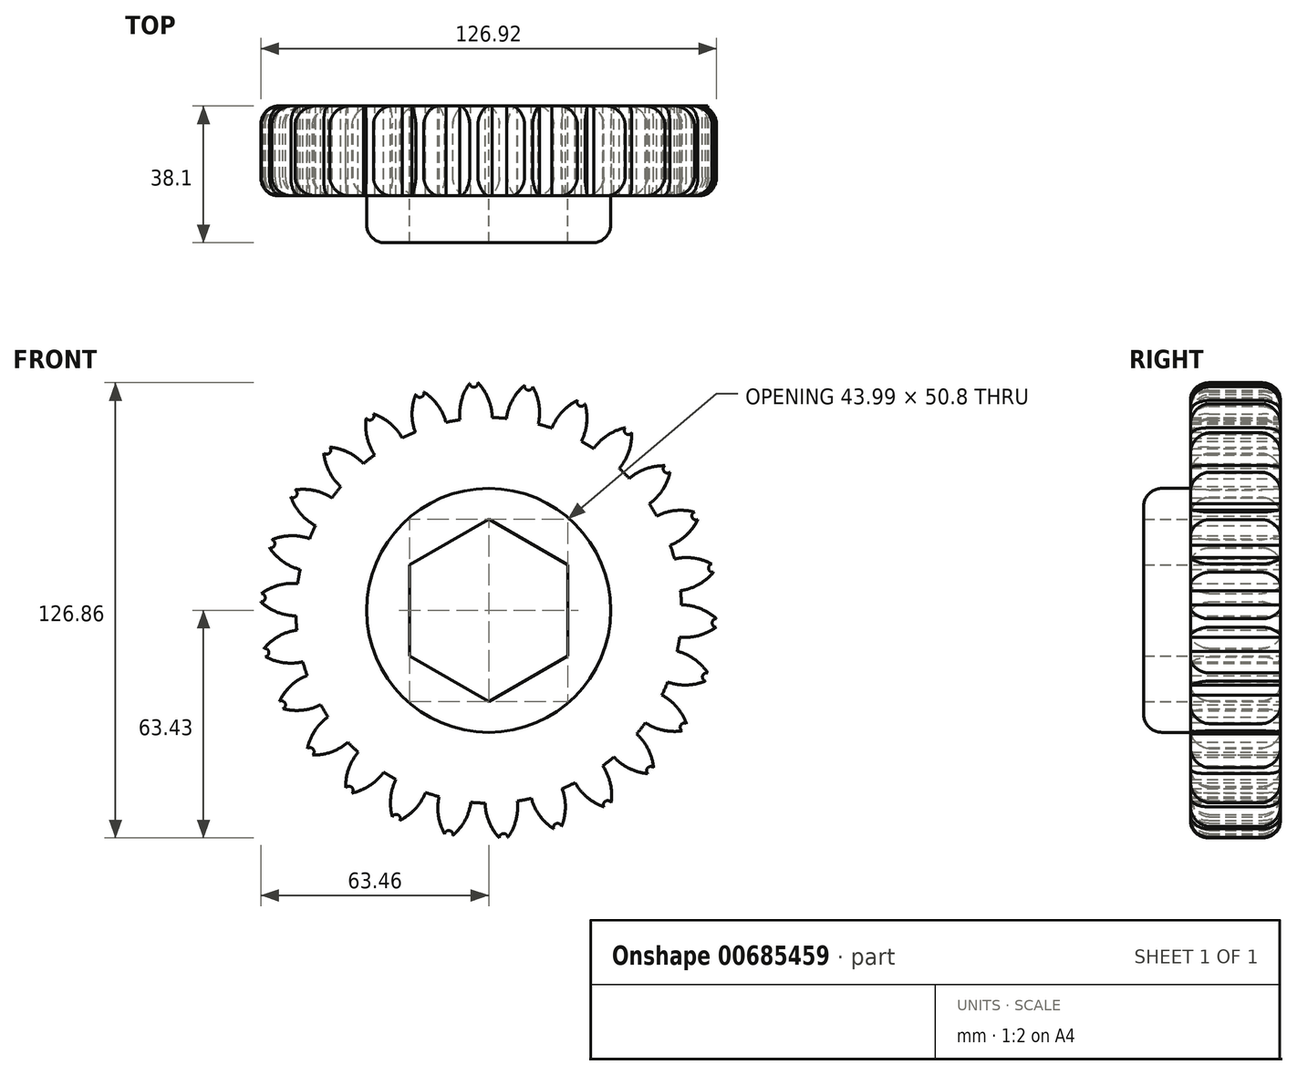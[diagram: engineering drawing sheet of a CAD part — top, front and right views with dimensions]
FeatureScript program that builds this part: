
annotation { "Feature Type Name" : "Feature", "Feature Type Description" : "" }
export const myFeature = defineFeature(function(context is Context, id is Id, definition is map)
    precondition{}
    {
        {
            var Q0;
            Q0=qCreatedBy(makeId("Front.planeOp"),FACE);
            var sketch = newSketch(context, id + "F0", { "sketchPlane" : qUnion([Q0])});
            skCircle(sketch, "E0", {"center": v(0, 0) * mm, "radius": 63.5 * mm, "construction": true});
            skCircle(sketch, "E1", {"center": v(0, 0) * mm, "radius": 58.67 * mm, "construction": true});
            skCircle(sketch, "E2", {"center": v(0, 0) * mm, "radius": 53.72 * mm});
            skLineSegment(sketch, "E3", {"start": v(0, 0) * mm, "end": v(0, 115.56) * mm, "construction": true});
            skLineSegment(sketch, "E4", {"start": v(0, 0) * mm, "end": v(-7.73, 117.88) * mm, "construction": true});
            skLineSegment(sketch, "E5", {"start": v(0, 58.67) * mm, "end": v(-76.77, 58.67) * mm, "construction": true});
            skLineSegment(sketch, "E6", {"start": v(0, 58.67) * mm, "end": v(-76.77, 30.73) * mm, "construction": true});
            skCircle(sketch, "E7", {"center": v(0, 0) * mm, "radius": 55.14 * mm, "construction": true});
            skCircle(sketch, "E8", {"center": v(0, 58.67) * mm, "radius": 14.6 * mm, "construction": true});
            skCircle(sketch, "E9", {"center": v(-13.63, 53.42) * mm, "radius": 14.6 * mm, "construction": true});
            skArc(sketch, "E10", {"start": v(0, 58.67) * mm, "mid": v(-1.27, 61.2) * mm, "end": v(-2.99, 63.43) * mm});
            skArc(sketch, "E11", {"start": v(0.97, 53.71) * mm, "mid": v(0.7, 56.24) * mm, "end": v(0, 58.67) * mm});
            skArc(sketch, "E12.MirrorCS", {"start": v(-7.66, 58.17) * mm, "mid": v(-6.73, 60.84) * mm, "end": v(-5.32, 63.28) * mm});
            skArc(sketch, "E13.MirrorCS", {"start": v(-7.98, 53.13) * mm, "mid": v(-8.04, 55.66) * mm, "end": v(-7.66, 58.17) * mm});
            skArc(sketch, "E14", {"start": v(-5.32, 63.28) * mm, "mid": v(-4.08, 62.2) * mm, "end": v(-2.99, 63.43) * mm});
            skPoint(sketch, "E15.0.midPoint", {"position": v(22.97, -13.77) * mm});
            skPoint(sketch, "E16.0.midPoint", {"position": v(19.49, -6.33) * mm});
            skCircle(sketch, "E17.cCircle", {"center": v(0, 0) * mm, "radius": 22 * mm, "construction": true});
            skLineSegment(sketch, "E17.0", {"start": v(22, 12.7) * mm, "end": v(22, -12.7) * mm});
            skLineSegment(sketch, "E17.1", {"start": v(22, -12.7) * mm, "end": v(0, -25.4) * mm});
            skLineSegment(sketch, "E17.2", {"start": v(0, -25.4) * mm, "end": v(-22, -12.7) * mm});
            skLineSegment(sketch, "E17.3", {"start": v(-22, -12.7) * mm, "end": v(-22, 12.7) * mm});
            skLineSegment(sketch, "E17.4", {"start": v(-22, 12.7) * mm, "end": v(0, 25.4) * mm});
            skLineSegment(sketch, "E17.5", {"start": v(0, 25.4) * mm, "end": v(22, 12.7) * mm});
            skPoint(sketch, "E17.0.midPoint", {"position": v(22, 0) * mm});
            skCircle(sketch, "E18", {"center": v(0, 0) * mm, "radius": 33.98 * mm});
            skSolve(sketch);
        }
        {
            var Q0;
            {var subQ0=sQuery(id+"F0.wireOp",EDGE,"E2");var subQ1=makeQuery(id+"F0.imprint","INTERSECT",VERTEX,{"derivedFrom":[subQ0,sQuery(id+"F0.wireOp",EDGE,"E11")]});Q0=makeQuery(id+"F0.imprint","IMPRINT",FACE,{"disambiguationData":[TD([[makeQuery(id+"F0.imprint","IMPRINT",EDGE,{"disambiguationData":[TD([[subQ1,-1.0]])],"derivedFrom":subQ0}),1.0]])]});}
            var Q1;
            Q1=makeQuery(id+"F0.imprint","IMPRINT",FACE,{"disambiguationData":[TD([[makeQuery(id+"F0.imprint","IMPRINT",EDGE,{"derivedFrom":sQuery(id+"F0.wireOp",EDGE,"E10")}),1.0]])]});
            extrude(context, id + "F1", {"entities" : qUnion([Q0, Q1]), "depth" : 25 * mm, "offsetDistance" : 25.4 * mm});
        }
        {
            var Q0;
            Q0=makeQuery(id+"F1.opExtrude","SWEPT_BODY",BODY,{"disambiguationData":[OSD([sQuery(id+"F0.wireOp",EDGE,"E2"),sQuery(id+"F0.wireOp",EDGE,"E10"),sQuery(id+"F0.wireOp",EDGE,"E11"),sQuery(id+"F0.wireOp",EDGE,"E12.MirrorCS"),sQuery(id+"F0.wireOp",EDGE,"E13.MirrorCS"),sQuery(id+"F0.wireOp",EDGE,"E14")])]});
            var Q1;
            Q1=makeQuery(id+"F1.opExtrude","SWEPT_FACE",FACE,{"disambiguationData":[OSD([sQuery(id+"F0.wireOp",EDGE,"E2")])]});
            circularPattern(context, id + "F2", {"entities" : qUnion([Q0]), "axis" : qUnion([Q1]), "angle" : 360 * degree, "instanceCount" : 26, "equalSpace" : true});
        }
        {
            var Q0;
            Q0=makeQuery(id+"F1.opExtrude","CAP_EDGE",EDGE,{"disambiguationData":[OSD([sQuery(id+"F0.wireOp",EDGE,"E14")])],"isStart":false});
            var Q1;
            Q1=makeQuery(id+"F1.opExtrude","CAP_EDGE",EDGE,{"disambiguationData":[OSD([sQuery(id+"F0.wireOp",EDGE,"E14")])],"isStart":true});
            var Q2;
            Q2=makeQuery(id+"F2.opPattern","COPY",EDGE,{"derivedFrom":makeQuery(id+"F1.opExtrude","CAP_EDGE",EDGE,{"disambiguationData":[OSD([sQuery(id+"F0.wireOp",EDGE,"E14")])],"isStart":false}),"instanceName":"25"});
            var Q3;
            Q3=makeQuery(id+"F2.opPattern","COPY",EDGE,{"derivedFrom":makeQuery(id+"F1.opExtrude","CAP_EDGE",EDGE,{"disambiguationData":[OSD([sQuery(id+"F0.wireOp",EDGE,"E14")])],"isStart":true}),"instanceName":"25"});
            var Q4;
            Q4=makeQuery(id+"F2.opPattern","COPY",EDGE,{"derivedFrom":makeQuery(id+"F1.opExtrude","CAP_EDGE",EDGE,{"disambiguationData":[OSD([sQuery(id+"F0.wireOp",EDGE,"E14")])],"isStart":true}),"instanceName":"24"});
            var Q5;
            Q5=makeQuery(id+"F2.opPattern","COPY",EDGE,{"derivedFrom":makeQuery(id+"F1.opExtrude","CAP_EDGE",EDGE,{"disambiguationData":[OSD([sQuery(id+"F0.wireOp",EDGE,"E14")])],"isStart":false}),"instanceName":"24"});
            var Q6;
            Q6=makeQuery(id+"F2.opPattern","COPY",EDGE,{"derivedFrom":makeQuery(id+"F1.opExtrude","CAP_EDGE",EDGE,{"disambiguationData":[OSD([sQuery(id+"F0.wireOp",EDGE,"E14")])],"isStart":false}),"instanceName":"23"});
            var Q7;
            Q7=makeQuery(id+"F2.opPattern","COPY",EDGE,{"derivedFrom":makeQuery(id+"F1.opExtrude","CAP_EDGE",EDGE,{"disambiguationData":[OSD([sQuery(id+"F0.wireOp",EDGE,"E14")])],"isStart":true}),"instanceName":"23"});
            var Q8;
            Q8=makeQuery(id+"F2.opPattern","COPY",EDGE,{"derivedFrom":makeQuery(id+"F1.opExtrude","CAP_EDGE",EDGE,{"disambiguationData":[OSD([sQuery(id+"F0.wireOp",EDGE,"E14")])],"isStart":false}),"instanceName":"22"});
            var Q9;
            Q9=makeQuery(id+"F2.opPattern","COPY",EDGE,{"derivedFrom":makeQuery(id+"F1.opExtrude","CAP_EDGE",EDGE,{"disambiguationData":[OSD([sQuery(id+"F0.wireOp",EDGE,"E14")])],"isStart":true}),"instanceName":"22"});
            var Q10;
            Q10=makeQuery(id+"F2.opPattern","COPY",EDGE,{"derivedFrom":makeQuery(id+"F1.opExtrude","CAP_EDGE",EDGE,{"disambiguationData":[OSD([sQuery(id+"F0.wireOp",EDGE,"E14")])],"isStart":true}),"instanceName":"21"});
            var Q11;
            Q11=makeQuery(id+"F2.opPattern","COPY",EDGE,{"derivedFrom":makeQuery(id+"F1.opExtrude","CAP_EDGE",EDGE,{"disambiguationData":[OSD([sQuery(id+"F0.wireOp",EDGE,"E14")])],"isStart":false}),"instanceName":"21"});
            var Q12;
            Q12=makeQuery(id+"F2.opPattern","COPY",EDGE,{"derivedFrom":makeQuery(id+"F1.opExtrude","CAP_EDGE",EDGE,{"disambiguationData":[OSD([sQuery(id+"F0.wireOp",EDGE,"E14")])],"isStart":true}),"instanceName":"20"});
            var Q13;
            Q13=makeQuery(id+"F2.opPattern","COPY",EDGE,{"derivedFrom":makeQuery(id+"F1.opExtrude","CAP_EDGE",EDGE,{"disambiguationData":[OSD([sQuery(id+"F0.wireOp",EDGE,"E14")])],"isStart":false}),"instanceName":"20"});
            var Q14;
            Q14=makeQuery(id+"F2.opPattern","COPY",EDGE,{"derivedFrom":makeQuery(id+"F1.opExtrude","CAP_EDGE",EDGE,{"disambiguationData":[OSD([sQuery(id+"F0.wireOp",EDGE,"E14")])],"isStart":true}),"instanceName":"19"});
            var Q15;
            Q15=makeQuery(id+"F2.opPattern","COPY",EDGE,{"derivedFrom":makeQuery(id+"F1.opExtrude","CAP_EDGE",EDGE,{"disambiguationData":[OSD([sQuery(id+"F0.wireOp",EDGE,"E14")])],"isStart":false}),"instanceName":"19"});
            var Q16;
            Q16=makeQuery(id+"F2.opPattern","COPY",EDGE,{"derivedFrom":makeQuery(id+"F1.opExtrude","CAP_EDGE",EDGE,{"disambiguationData":[OSD([sQuery(id+"F0.wireOp",EDGE,"E14")])],"isStart":true}),"instanceName":"18"});
            var Q17;
            Q17=makeQuery(id+"F2.opPattern","COPY",EDGE,{"derivedFrom":makeQuery(id+"F1.opExtrude","CAP_EDGE",EDGE,{"disambiguationData":[OSD([sQuery(id+"F0.wireOp",EDGE,"E14")])],"isStart":false}),"instanceName":"18"});
            var Q18;
            Q18=makeQuery(id+"F2.opPattern","COPY",EDGE,{"derivedFrom":makeQuery(id+"F1.opExtrude","CAP_EDGE",EDGE,{"disambiguationData":[OSD([sQuery(id+"F0.wireOp",EDGE,"E14")])],"isStart":true}),"instanceName":"17"});
            var Q19;
            Q19=makeQuery(id+"F2.opPattern","COPY",EDGE,{"derivedFrom":makeQuery(id+"F1.opExtrude","CAP_EDGE",EDGE,{"disambiguationData":[OSD([sQuery(id+"F0.wireOp",EDGE,"E14")])],"isStart":false}),"instanceName":"17"});
            var Q20;
            Q20=makeQuery(id+"F2.opPattern","COPY",EDGE,{"derivedFrom":makeQuery(id+"F1.opExtrude","CAP_EDGE",EDGE,{"disambiguationData":[OSD([sQuery(id+"F0.wireOp",EDGE,"E14")])],"isStart":false}),"instanceName":"16"});
            var Q21;
            Q21=makeQuery(id+"F2.opPattern","COPY",EDGE,{"derivedFrom":makeQuery(id+"F1.opExtrude","CAP_EDGE",EDGE,{"disambiguationData":[OSD([sQuery(id+"F0.wireOp",EDGE,"E14")])],"isStart":true}),"instanceName":"16"});
            var Q22;
            Q22=makeQuery(id+"F2.opPattern","COPY",EDGE,{"derivedFrom":makeQuery(id+"F1.opExtrude","CAP_EDGE",EDGE,{"disambiguationData":[OSD([sQuery(id+"F0.wireOp",EDGE,"E14")])],"isStart":true}),"instanceName":"15"});
            var Q23;
            Q23=makeQuery(id+"F2.opPattern","COPY",EDGE,{"derivedFrom":makeQuery(id+"F1.opExtrude","CAP_EDGE",EDGE,{"disambiguationData":[OSD([sQuery(id+"F0.wireOp",EDGE,"E14")])],"isStart":false}),"instanceName":"15"});
            var Q24;
            Q24=makeQuery(id+"F2.opPattern","COPY",EDGE,{"derivedFrom":makeQuery(id+"F1.opExtrude","CAP_EDGE",EDGE,{"disambiguationData":[OSD([sQuery(id+"F0.wireOp",EDGE,"E14")])],"isStart":true}),"instanceName":"14"});
            var Q25;
            Q25=makeQuery(id+"F2.opPattern","COPY",EDGE,{"derivedFrom":makeQuery(id+"F1.opExtrude","CAP_EDGE",EDGE,{"disambiguationData":[OSD([sQuery(id+"F0.wireOp",EDGE,"E14")])],"isStart":false}),"instanceName":"14"});
            var Q26;
            Q26=makeQuery(id+"F2.opPattern","COPY",EDGE,{"derivedFrom":makeQuery(id+"F1.opExtrude","CAP_EDGE",EDGE,{"disambiguationData":[OSD([sQuery(id+"F0.wireOp",EDGE,"E14")])],"isStart":true}),"instanceName":"13"});
            var Q27;
            Q27=makeQuery(id+"F2.opPattern","COPY",EDGE,{"derivedFrom":makeQuery(id+"F1.opExtrude","CAP_EDGE",EDGE,{"disambiguationData":[OSD([sQuery(id+"F0.wireOp",EDGE,"E14")])],"isStart":false}),"instanceName":"13"});
            var Q28;
            Q28=makeQuery(id+"F2.opPattern","COPY",EDGE,{"derivedFrom":makeQuery(id+"F1.opExtrude","CAP_EDGE",EDGE,{"disambiguationData":[OSD([sQuery(id+"F0.wireOp",EDGE,"E14")])],"isStart":false}),"instanceName":"12"});
            var Q29;
            Q29=makeQuery(id+"F2.opPattern","COPY",EDGE,{"derivedFrom":makeQuery(id+"F1.opExtrude","CAP_EDGE",EDGE,{"disambiguationData":[OSD([sQuery(id+"F0.wireOp",EDGE,"E14")])],"isStart":true}),"instanceName":"12"});
            var Q30;
            Q30=makeQuery(id+"F2.opPattern","COPY",EDGE,{"derivedFrom":makeQuery(id+"F1.opExtrude","CAP_EDGE",EDGE,{"disambiguationData":[OSD([sQuery(id+"F0.wireOp",EDGE,"E14")])],"isStart":true}),"instanceName":"11"});
            var Q31;
            Q31=makeQuery(id+"F2.opPattern","COPY",EDGE,{"derivedFrom":makeQuery(id+"F1.opExtrude","CAP_EDGE",EDGE,{"disambiguationData":[OSD([sQuery(id+"F0.wireOp",EDGE,"E14")])],"isStart":false}),"instanceName":"11"});
            var Q32;
            Q32=makeQuery(id+"F2.opPattern","COPY",EDGE,{"derivedFrom":makeQuery(id+"F1.opExtrude","CAP_EDGE",EDGE,{"disambiguationData":[OSD([sQuery(id+"F0.wireOp",EDGE,"E14")])],"isStart":true}),"instanceName":"10"});
            var Q33;
            Q33=makeQuery(id+"F2.opPattern","COPY",EDGE,{"derivedFrom":makeQuery(id+"F1.opExtrude","CAP_EDGE",EDGE,{"disambiguationData":[OSD([sQuery(id+"F0.wireOp",EDGE,"E14")])],"isStart":false}),"instanceName":"10"});
            var Q34;
            Q34=makeQuery(id+"F2.opPattern","COPY",EDGE,{"derivedFrom":makeQuery(id+"F1.opExtrude","CAP_EDGE",EDGE,{"disambiguationData":[OSD([sQuery(id+"F0.wireOp",EDGE,"E14")])],"isStart":true}),"instanceName":"9"});
            var Q35;
            Q35=makeQuery(id+"F2.opPattern","COPY",EDGE,{"derivedFrom":makeQuery(id+"F1.opExtrude","CAP_EDGE",EDGE,{"disambiguationData":[OSD([sQuery(id+"F0.wireOp",EDGE,"E14")])],"isStart":false}),"instanceName":"9"});
            var Q36;
            Q36=makeQuery(id+"F2.opPattern","COPY",EDGE,{"derivedFrom":makeQuery(id+"F1.opExtrude","CAP_EDGE",EDGE,{"disambiguationData":[OSD([sQuery(id+"F0.wireOp",EDGE,"E14")])],"isStart":false}),"instanceName":"8"});
            var Q37;
            Q37=makeQuery(id+"F2.opPattern","COPY",EDGE,{"derivedFrom":makeQuery(id+"F1.opExtrude","CAP_EDGE",EDGE,{"disambiguationData":[OSD([sQuery(id+"F0.wireOp",EDGE,"E14")])],"isStart":true}),"instanceName":"7"});
            var Q38;
            Q38=makeQuery(id+"F2.opPattern","COPY",EDGE,{"derivedFrom":makeQuery(id+"F1.opExtrude","CAP_EDGE",EDGE,{"disambiguationData":[OSD([sQuery(id+"F0.wireOp",EDGE,"E14")])],"isStart":false}),"instanceName":"7"});
            var Q39;
            Q39=makeQuery(id+"F2.opPattern","COPY",EDGE,{"derivedFrom":makeQuery(id+"F1.opExtrude","CAP_EDGE",EDGE,{"disambiguationData":[OSD([sQuery(id+"F0.wireOp",EDGE,"E14")])],"isStart":true}),"instanceName":"6"});
            var Q40;
            Q40=makeQuery(id+"F2.opPattern","COPY",EDGE,{"derivedFrom":makeQuery(id+"F1.opExtrude","CAP_EDGE",EDGE,{"disambiguationData":[OSD([sQuery(id+"F0.wireOp",EDGE,"E14")])],"isStart":false}),"instanceName":"6"});
            var Q41;
            Q41=makeQuery(id+"F2.opPattern","COPY",EDGE,{"derivedFrom":makeQuery(id+"F1.opExtrude","CAP_EDGE",EDGE,{"disambiguationData":[OSD([sQuery(id+"F0.wireOp",EDGE,"E14")])],"isStart":true}),"instanceName":"5"});
            var Q42;
            Q42=makeQuery(id+"F2.opPattern","COPY",EDGE,{"derivedFrom":makeQuery(id+"F1.opExtrude","CAP_EDGE",EDGE,{"disambiguationData":[OSD([sQuery(id+"F0.wireOp",EDGE,"E14")])],"isStart":false}),"instanceName":"5"});
            var Q43;
            Q43=makeQuery(id+"F2.opPattern","COPY",EDGE,{"derivedFrom":makeQuery(id+"F1.opExtrude","CAP_EDGE",EDGE,{"disambiguationData":[OSD([sQuery(id+"F0.wireOp",EDGE,"E14")])],"isStart":true}),"instanceName":"4"});
            var Q44;
            Q44=makeQuery(id+"F2.opPattern","COPY",EDGE,{"derivedFrom":makeQuery(id+"F1.opExtrude","CAP_EDGE",EDGE,{"disambiguationData":[OSD([sQuery(id+"F0.wireOp",EDGE,"E14")])],"isStart":false}),"instanceName":"4"});
            var Q45;
            Q45=makeQuery(id+"F2.opPattern","COPY",EDGE,{"derivedFrom":makeQuery(id+"F1.opExtrude","CAP_EDGE",EDGE,{"disambiguationData":[OSD([sQuery(id+"F0.wireOp",EDGE,"E14")])],"isStart":true}),"instanceName":"3"});
            var Q46;
            Q46=makeQuery(id+"F2.opPattern","COPY",EDGE,{"derivedFrom":makeQuery(id+"F1.opExtrude","CAP_EDGE",EDGE,{"disambiguationData":[OSD([sQuery(id+"F0.wireOp",EDGE,"E14")])],"isStart":false}),"instanceName":"3"});
            var Q47;
            Q47=makeQuery(id+"F2.opPattern","COPY",EDGE,{"derivedFrom":makeQuery(id+"F1.opExtrude","CAP_EDGE",EDGE,{"disambiguationData":[OSD([sQuery(id+"F0.wireOp",EDGE,"E14")])],"isStart":true}),"instanceName":"2"});
            var Q48;
            Q48=makeQuery(id+"F2.opPattern","COPY",EDGE,{"derivedFrom":makeQuery(id+"F1.opExtrude","CAP_EDGE",EDGE,{"disambiguationData":[OSD([sQuery(id+"F0.wireOp",EDGE,"E14")])],"isStart":false}),"instanceName":"2"});
            var Q49;
            Q49=makeQuery(id+"F2.opPattern","COPY",EDGE,{"derivedFrom":makeQuery(id+"F1.opExtrude","CAP_EDGE",EDGE,{"disambiguationData":[OSD([sQuery(id+"F0.wireOp",EDGE,"E14")])],"isStart":true}),"instanceName":"1"});
            var Q50;
            Q50=makeQuery(id+"F2.opPattern","COPY",EDGE,{"derivedFrom":makeQuery(id+"F1.opExtrude","CAP_EDGE",EDGE,{"disambiguationData":[OSD([sQuery(id+"F0.wireOp",EDGE,"E14")])],"isStart":false}),"instanceName":"1"});
            var Q51;
            Q51=makeQuery(id+"FiH3POfzxQtOGoF_1.opExtrude","CAP_EDGE",EDGE,{"disambiguationData":[OSD([sQuery(id+"FlN3JYI4IPwnwes_1.wireOp",EDGE,"wg0dXFDc-mmLY-1UWq-sbby-NMdXq94I11Wg")])],"isStart":false});
            fillet(context, id + "F3", {"entities" : qUnion([Q0, Q1, Q2, Q3, Q4, Q5, Q6, Q7, Q8, Q9, Q10, Q11, Q12, Q13, Q14, Q15, Q16, Q17, Q18, Q19, Q20, Q21, Q22, Q23, Q24, Q25, Q26, Q27, Q28, Q29, Q30, Q31, Q32, Q33, Q34, Q35, Q36, Q37, Q38, Q39, Q40, Q41, Q42, Q43, Q44, Q45, Q46, Q47, Q48, Q49, Q50, Q51]), "radius" : 5.08 * mm, "tangentPropagation" : true, "allowEdgeOverflow" : false});
        }
        {
            var Q0;
            Q0=makeQuery(id+"F0.imprint","IMPRINT",FACE,{"disambiguationData":[TD([[makeQuery(id+"F0.imprint","IMPRINT",EDGE,{"derivedFrom":sQuery(id+"F0.wireOp",EDGE,"E17.0")}),1.0]])]});
            extrude(context, id + "F4", {"entities" : qUnion([Q0]), "operationType" : NewBodyOperationType.ADD, "depth" : 38.1 * mm, "offsetDistance" : 25.4 * mm});
        }
        {
            var Q0;
            Q0=makeQuery(id+"F4.opExtrude","CAP_EDGE",EDGE,{"disambiguationData":[OSD([sQuery(id+"F0.wireOp",EDGE,"E18")])],"isStart":false});
            fillet(context, id + "F5", {"entities" : qUnion([Q0]), "radius" : 5.08 * mm, "tangentPropagation" : true, "allowEdgeOverflow" : false});
        }
    });
